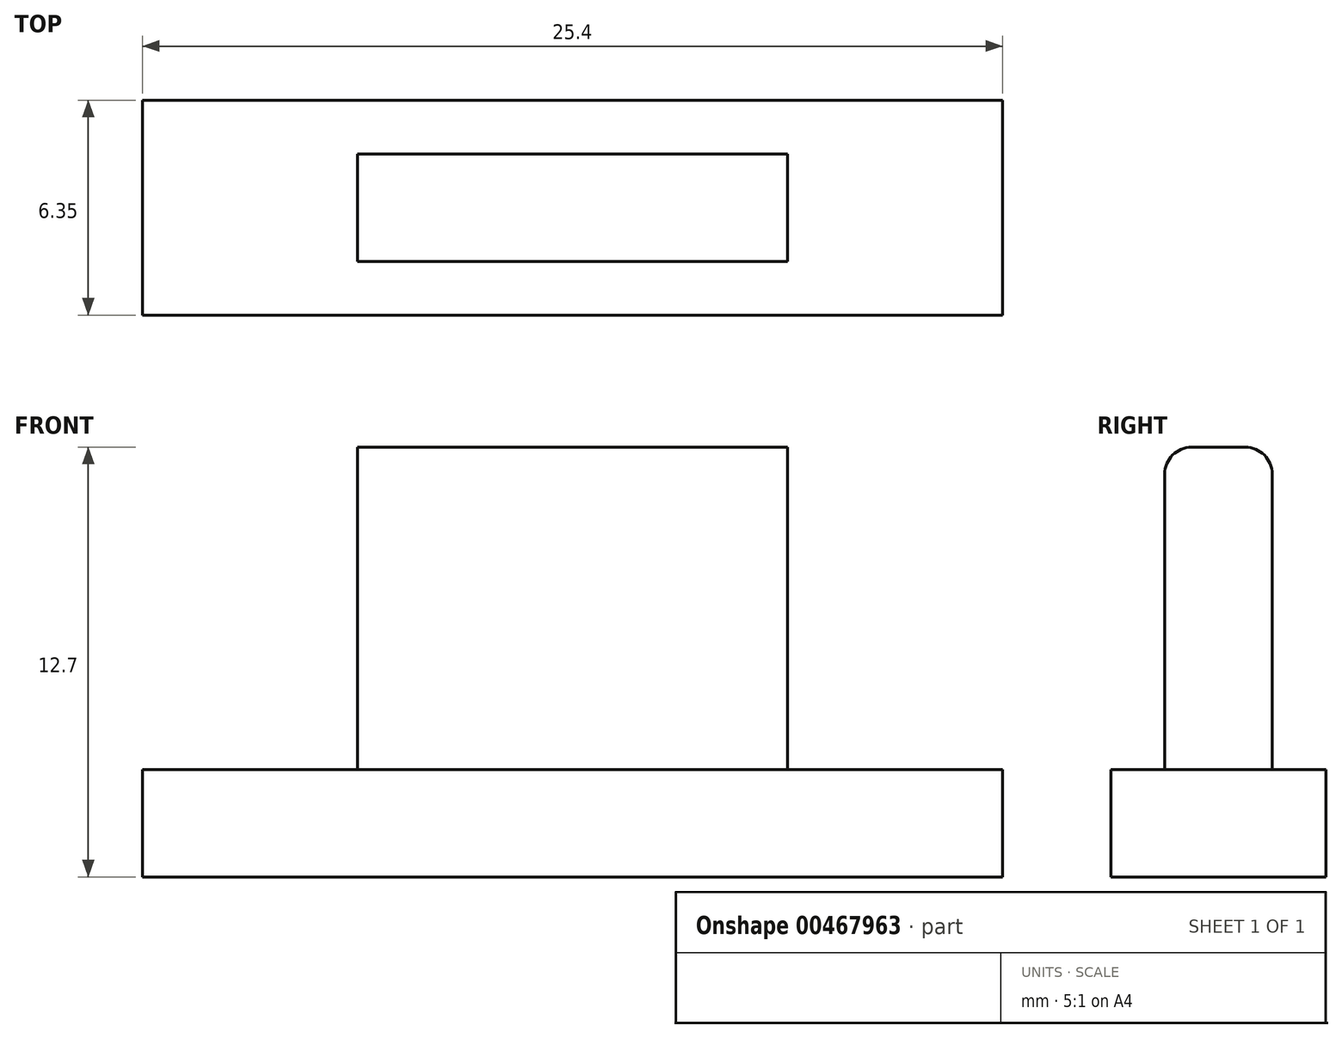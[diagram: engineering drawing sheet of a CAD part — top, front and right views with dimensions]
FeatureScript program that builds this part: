
annotation { "Feature Type Name" : "Feature", "Feature Type Description" : "" }
export const myFeature = defineFeature(function(context is Context, id is Id, definition is map)
    precondition{}
    {
        {
            var Q0;
            Q0=qCreatedBy(makeId("Top.planeOp"),FACE);
            var sketch = newSketch(context, id + "F0", { "sketchPlane" : qUnion([Q0])});
            skLineSegment(sketch, "E0.bottom", {"start": v(-12.7, 0) * mm, "end": v(12.7, 0) * mm});
            skLineSegment(sketch, "E0.top", {"start": v(-12.7, -6.35) * mm, "end": v(12.7, -6.35) * mm});
            skLineSegment(sketch, "E0.left", {"start": v(-12.7, 0) * mm, "end": v(-12.7, -6.35) * mm});
            skLineSegment(sketch, "E0.right", {"start": v(12.7, 0) * mm, "end": v(12.7, -6.35) * mm});
            skLineSegment(sketch, "E1.bottom", {"start": v(-3.18, 0) * mm, "end": v(3.18, 0) * mm});
            skLineSegment(sketch, "E1.top", {"start": v(-3.18, 12.7) * mm, "end": v(3.18, 12.7) * mm});
            skLineSegment(sketch, "E1.left", {"start": v(-3.18, 0) * mm, "end": v(-3.18, 12.7) * mm});
            skLineSegment(sketch, "E1.right", {"start": v(3.17, 0) * mm, "end": v(3.17, 12.7) * mm});
            skLineSegment(sketch, "E2.bottom", {"start": v(-6.35, -1.59) * mm, "end": v(6.35, -1.59) * mm});
            skLineSegment(sketch, "E2.top", {"start": v(-6.35, -4.76) * mm, "end": v(6.35, -4.76) * mm});
            skLineSegment(sketch, "E2.left", {"start": v(-6.35, -1.59) * mm, "end": v(-6.35, -4.76) * mm});
            skLineSegment(sketch, "E2.right", {"start": v(6.35, -1.59) * mm, "end": v(6.35, -4.76) * mm});
            skSolve(sketch);
        }
        {
            var Q0;
            Q0=makeQuery(id+"F0.imprint","IMPRINT",FACE,{"disambiguationData":[TD([[makeQuery(id+"F0.imprint","IMPRINT",EDGE,{"derivedFrom":sQuery(id+"F0.wireOp",EDGE,"E0.top")}),1.0]])]});
            var Q1;
            Q1=makeQuery(id+"F0.imprint","IMPRINT",FACE,{"disambiguationData":[TD([[makeQuery(id+"F0.imprint","IMPRINT",EDGE,{"derivedFrom":sQuery(id+"F0.wireOp",EDGE,"E2.bottom")}),-1.0]])]});
            var Q2;
            Q2=makeQuery(id+"F0.imprint","IMPRINT",FACE,{"disambiguationData":[TD([[makeQuery(id+"F0.imprint","IMPRINT",EDGE,{"derivedFrom":sQuery(id+"F0.wireOp",EDGE,"E1.bottom")}),1.0]])]});
            extrude(context, id + "F1", {"entities" : qUnion([Q0, Q1, Q2]), "oppositeDirection" : true, "depth" : 3.17 * mm, "offsetDistance" : 25.4 * mm});
        }
        {
            var Q0;
            Q0=makeQuery(id+"F0.imprint","IMPRINT",FACE,{"disambiguationData":[TD([[makeQuery(id+"F0.imprint","IMPRINT",EDGE,{"derivedFrom":sQuery(id+"F0.wireOp",EDGE,"E2.bottom")}),-1.0]])]});
            extrude(context, id + "F2", {"entities" : qUnion([Q0]), "operationType" : NewBodyOperationType.ADD, "depth" : 9.52 * mm, "offsetDistance" : 25.4 * mm});
        }
        {
            var Q0;
            Q0=makeQuery(id+"F2.opExtrude","CAP_EDGE",EDGE,{"disambiguationData":[OSD([sQuery(id+"F0.wireOp",EDGE,"E2.top")])],"isStart":false});
            var Q1;
            Q1=makeQuery(id+"F2.opExtrude","CAP_EDGE",EDGE,{"disambiguationData":[OSD([sQuery(id+"F0.wireOp",EDGE,"E2.bottom")])],"isStart":false});
            var Q2;
            Q2=makeQuery(id+"F2.opExtrude","CAP_EDGE",EDGE,{"disambiguationData":[OSD([sQuery(id+"F0.wireOp",EDGE,"E2.bottom")])],"isStart":true});
            var Q3;
            Q3=makeQuery(id+"F2.opExtrude","CAP_EDGE",EDGE,{"disambiguationData":[OSD([sQuery(id+"F0.wireOp",EDGE,"E2.top")])],"isStart":true});
            fillet(context, id + "F3", {"entities" : qUnion([Q0, Q1, Q2, Q3]), "radius" : 0.8 * mm, "tangentPropagation" : true, "allowEdgeOverflow" : false});
        }
    });
